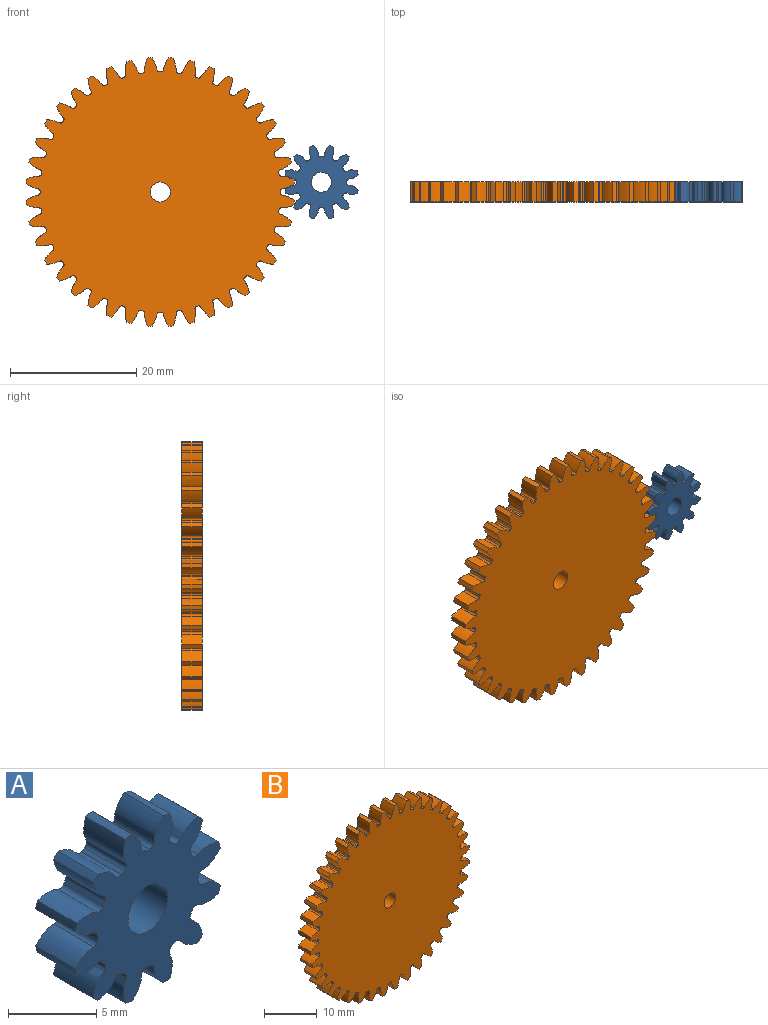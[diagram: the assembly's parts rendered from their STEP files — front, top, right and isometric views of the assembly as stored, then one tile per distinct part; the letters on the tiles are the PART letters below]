
ASSEMBLY  parts=2 mates=1
PART A: 75 faces, bbox 11.6x3.2x11.6 mm
  f0: cylinder r=5.93mm len=3.18mm, axis (0,1,0), area 1.7mm2, adj f11,f14,f60,f72
  f1: cylinder r=5.93mm len=3.18mm, axis (0,1,0), area 1.7mm2, adj f11,f14,f67,f70
  f2: cylinder r=5.93mm len=3.18mm, axis (0,1,0), area 1.7mm2, adj f11,f14,f55,f62
  f3: cylinder r=5.93mm len=3.18mm, axis (0,1,0), area 1.7mm2, adj f11,f14,f50,f57
  f4: cylinder r=5.93mm len=3.18mm, axis (0,1,0), area 1.7mm2, adj f11,f14,f45,f52
  f5: cylinder r=5.93mm len=3.18mm, axis (0,1,0), area 1.7mm2, adj f11,f14,f35,f47
  f6: cylinder r=5.93mm len=3.18mm, axis (0,1,0), area 1.7mm2, adj f11,f14,f15,f42
  f7: cylinder r=5.93mm len=3.18mm, axis (0,1,0), area 1.7mm2, adj f11,f14,f37,f40
  f8: cylinder r=5.93mm len=3.18mm, axis (0,1,0), area 1.7mm2, adj f11,f14,f25,f32
  f9: cylinder r=5.93mm len=3.18mm, axis (0,1,0), area 1.7mm2, adj f11,f14,f20,f27
  f10: cylinder r=5.93mm len=3.18mm, axis (0,1,0), area 1.7mm2, adj f11,f14,f22,f65
  f11: plane 11.6x11.6mm, normal (0,-1,0), area 70.2mm2, adj f0,f1,f2,f3,f4,f5,f6,f7
  f12: cylinder r=1.59mm len=3.18mm, axis (0,1,0), area 31.7mm2, adj f11,f14
  f13: cylinder r=5.93mm len=3.18mm, axis (0,1,0), area 1.7mm2, adj f11,f14,f17,f30
  f14: plane 11.6x11.6mm, normal (0,1,0), area 70.2mm2, adj f0,f1,f2,f3,f4,f5,f6,f7
  f15: extruded ~3.18x1.46mm, area 5.4mm2, adj f6,f11,f14,f18
  f16: cylinder r=4.02mm len=3.18mm, axis (0,1,0), area 0.9mm2, adj f11,f14,f18,f19
  f17: extruded ~3.18x1.46mm, area 5.4mm2, adj f11,f13,f14,f19
  f18: cylinder r=0.35mm len=3.18mm, axis (0,1,0), area 1.7mm2, adj f11,f14,f15,f16
  f19: cylinder r=0.35mm len=3.18mm, axis (0,1,0), area 1.7mm2, adj f11,f14,f16,f17
  f20: extruded ~3.18x1.46mm, area 5.4mm2, adj f9,f11,f14,f23
  f21: cylinder r=4.02mm len=3.18mm, axis (0,1,0), area 0.9mm2, adj f11,f14,f23,f24
  f22: extruded ~3.18x1.46mm, area 5.4mm2, adj f10,f11,f14,f24
  f23: cylinder r=0.35mm len=3.18mm, axis (0,1,0), area 1.7mm2, adj f11,f14,f20,f21
  f24: cylinder r=0.35mm len=3.18mm, axis (0,1,0), area 1.7mm2, adj f11,f14,f21,f22
  f25: extruded ~3.18x1.4mm, area 5.4mm2, adj f8,f11,f14,f28
  f26: cylinder r=4.02mm len=3.18mm, axis (0,1,0), area 0.9mm2, adj f11,f14,f28,f29
  f27: extruded ~3.18x1.65mm, area 5.4mm2, adj f9,f11,f14,f29
  f28: cylinder r=0.35mm len=3.18mm, axis (0,1,0), area 1.7mm2, adj f11,f14,f25,f26
  f29: cylinder r=0.35mm len=3.18mm, axis (0,1,0), area 1.7mm2, adj f11,f14,f26,f27
  f30: extruded ~3.18x1.65mm, area 5.4mm2, adj f11,f13,f14,f33
  f31: cylinder r=4.02mm len=3.18mm, axis (0,1,0), area 0.9mm2, adj f11,f14,f33,f34
  f32: extruded ~3.18x1.4mm, area 5.4mm2, adj f8,f11,f14,f34
  f33: cylinder r=0.35mm len=3.18mm, axis (0,1,0), area 1.7mm2, adj f11,f14,f30,f31
  f34: cylinder r=0.35mm len=3.18mm, axis (0,1,0), area 1.7mm2, adj f11,f14,f31,f32
  f35: extruded ~3.18x1.65mm, area 5.4mm2, adj f5,f11,f14,f38
  f36: cylinder r=4.02mm len=3.18mm, axis (0,1,0), area 0.9mm2, adj f11,f14,f38,f39
  f37: extruded ~3.18x1.4mm, area 5.4mm2, adj f7,f11,f14,f39
  f38: cylinder r=0.35mm len=3.18mm, axis (0,1,0), area 1.7mm2, adj f11,f14,f35,f36
  f39: cylinder r=0.35mm len=3.18mm, axis (0,1,0), area 1.7mm2, adj f11,f14,f36,f37
  f40: extruded ~3.18x1.4mm, area 5.4mm2, adj f7,f11,f14,f43
  f41: cylinder r=4.02mm len=3.18mm, axis (0,1,0), area 0.9mm2, adj f11,f14,f43,f44
  f42: extruded ~3.18x1.65mm, area 5.4mm2, adj f6,f11,f14,f44
  f43: cylinder r=0.35mm len=3.18mm, axis (0,1,0), area 1.7mm2, adj f11,f14,f40,f41
  f44: cylinder r=0.35mm len=3.18mm, axis (0,1,0), area 1.7mm2, adj f11,f14,f41,f42
  f45: extruded ~3.18x1.46mm, area 5.4mm2, adj f4,f11,f14,f48
  f46: cylinder r=4.02mm len=3.18mm, axis (0,1,0), area 0.9mm2, adj f11,f14,f48,f49
  f47: extruded ~3.18x1.46mm, area 5.4mm2, adj f5,f11,f14,f49
  f48: cylinder r=0.35mm len=3.18mm, axis (0,1,0), area 1.7mm2, adj f11,f14,f45,f46
  f49: cylinder r=0.35mm len=3.18mm, axis (0,1,0), area 1.7mm2, adj f11,f14,f46,f47
  f50: extruded ~3.18x1.4mm, area 5.4mm2, adj f3,f11,f14,f53
  f51: cylinder r=4.02mm len=3.18mm, axis (0,1,0), area 0.9mm2, adj f11,f14,f53,f54
  f52: extruded ~3.18x1.65mm, area 5.4mm2, adj f4,f11,f14,f54
  f53: cylinder r=0.35mm len=3.18mm, axis (0,1,0), area 1.7mm2, adj f11,f14,f50,f51
  f54: cylinder r=0.35mm len=3.18mm, axis (0,1,0), area 1.7mm2, adj f11,f14,f51,f52
  f55: extruded ~3.18x1.65mm, area 5.4mm2, adj f2,f11,f14,f58
  f56: cylinder r=4.02mm len=3.18mm, axis (0,1,0), area 0.9mm2, adj f11,f14,f58,f59
  f57: extruded ~3.18x1.4mm, area 5.4mm2, adj f3,f11,f14,f59
  f58: cylinder r=0.35mm len=3.18mm, axis (0,1,0), area 1.7mm2, adj f11,f14,f55,f56
  f59: cylinder r=0.35mm len=3.18mm, axis (0,1,0), area 1.7mm2, adj f11,f14,f56,f57
  f60: extruded ~3.18x1.46mm, area 5.4mm2, adj f0,f11,f14,f63
  f61: cylinder r=4.02mm len=3.18mm, axis (0,1,0), area 0.9mm2, adj f11,f14,f63,f64
  f62: extruded ~3.18x1.46mm, area 5.4mm2, adj f2,f11,f14,f64
  f63: cylinder r=0.35mm len=3.18mm, axis (0,1,0), area 1.7mm2, adj f11,f14,f60,f61
  f64: cylinder r=0.35mm len=3.18mm, axis (0,1,0), area 1.7mm2, adj f11,f14,f61,f62
  f65: extruded ~3.18x1.65mm, area 5.4mm2, adj f10,f11,f14,f68
  f66: cylinder r=4.02mm len=3.18mm, axis (0,1,0), area 0.9mm2, adj f11,f14,f68,f69
  f67: extruded ~3.18x1.4mm, area 5.4mm2, adj f1,f11,f14,f69
  f68: cylinder r=0.35mm len=3.18mm, axis (0,1,0), area 1.7mm2, adj f11,f14,f65,f66
  f69: cylinder r=0.35mm len=3.18mm, axis (0,1,0), area 1.7mm2, adj f11,f14,f66,f67
  f70: extruded ~3.18x1.4mm, area 5.4mm2, adj f1,f11,f14,f73
  f71: cylinder r=4.02mm len=3.18mm, axis (0,1,0), area 0.9mm2, adj f11,f14,f73,f74
  f72: extruded ~3.18x1.65mm, area 5.4mm2, adj f0,f11,f14,f74
  f73: cylinder r=0.35mm len=3.18mm, axis (0,1,0), area 1.7mm2, adj f11,f14,f70,f71
  f74: cylinder r=0.35mm len=3.18mm, axis (0,1,0), area 1.7mm2, adj f11,f14,f71,f72
PART B: 243 faces, bbox 42.6x3.2x42.6 mm
  f0: cylinder r=21.34mm len=3.18mm, axis (0,1,0), area 2.5mm2, adj f39,f42,f148,f240
  f1: cylinder r=21.34mm len=3.18mm, axis (0,1,0), area 2.5mm2, adj f39,f42,f235,f238
  f2: cylinder r=21.34mm len=3.18mm, axis (0,1,0), area 2.5mm2, adj f39,f42,f230,f233
  f3: cylinder r=21.34mm len=3.18mm, axis (0,1,0), area 2.5mm2, adj f39,f42,f225,f228
  f4: cylinder r=21.34mm len=3.18mm, axis (0,1,0), area 2.5mm2, adj f39,f42,f220,f223
  f5: cylinder r=21.34mm len=3.18mm, axis (0,1,0), area 2.5mm2, adj f39,f42,f215,f218
  f6: cylinder r=21.34mm len=3.18mm, axis (0,1,0), area 2.5mm2, adj f39,f42,f210,f213
  f7: cylinder r=21.34mm len=3.18mm, axis (0,1,0), area 2.5mm2, adj f39,f42,f205,f208
  f8: cylinder r=21.34mm len=3.18mm, axis (0,1,0), area 2.5mm2, adj f39,f42,f193,f200
  f9: cylinder r=21.34mm len=3.18mm, axis (0,1,0), area 2.5mm2, adj f39,f42,f195,f203
  f10: cylinder r=21.34mm len=3.18mm, axis (0,1,0), area 2.5mm2, adj f39,f42,f190,f198
  f11: cylinder r=21.34mm len=3.18mm, axis (0,1,0), area 2.5mm2, adj f39,f42,f185,f188
  f12: cylinder r=21.34mm len=3.18mm, axis (0,1,0), area 2.5mm2, adj f39,f42,f180,f183
  f13: cylinder r=21.34mm len=3.18mm, axis (0,1,0), area 2.5mm2, adj f39,f42,f175,f178
  f14: cylinder r=21.34mm len=3.18mm, axis (0,1,0), area 2.5mm2, adj f39,f42,f170,f173
  f15: cylinder r=21.34mm len=3.18mm, axis (0,1,0), area 2.5mm2, adj f39,f42,f165,f168
  f16: cylinder r=21.34mm len=3.18mm, axis (0,1,0), area 2.5mm2, adj f39,f42,f138,f160
  f17: cylinder r=21.34mm len=3.18mm, axis (0,1,0), area 2.5mm2, adj f39,f42,f155,f158
  f18: cylinder r=21.34mm len=3.18mm, axis (0,1,0), area 2.5mm2, adj f39,f42,f143,f150
  f19: cylinder r=21.34mm len=3.18mm, axis (0,1,0), area 2.5mm2, adj f39,f42,f145,f153
  f20: cylinder r=21.34mm len=3.18mm, axis (0,1,0), area 2.5mm2, adj f39,f42,f133,f140
  f21: cylinder r=21.34mm len=3.18mm, axis (0,1,0), area 2.5mm2, adj f39,f42,f128,f135
  f22: cylinder r=21.34mm len=3.18mm, axis (0,1,0), area 2.5mm2, adj f39,f42,f123,f130
  f23: cylinder r=21.34mm len=3.18mm, axis (0,1,0), area 2.5mm2, adj f39,f42,f83,f125
  f24: cylinder r=21.34mm len=3.18mm, axis (0,1,0), area 2.5mm2, adj f39,f42,f43,f120
  f25: cylinder r=21.34mm len=3.18mm, axis (0,1,0), area 2.5mm2, adj f39,f42,f115,f118
  f26: cylinder r=21.34mm len=3.18mm, axis (0,1,0), area 2.5mm2, adj f39,f42,f110,f113
  f27: cylinder r=21.34mm len=3.18mm, axis (0,1,0), area 2.5mm2, adj f39,f42,f105,f108
  f28: cylinder r=21.34mm len=3.18mm, axis (0,1,0), area 2.5mm2, adj f39,f42,f93,f100
  f29: cylinder r=21.34mm len=3.18mm, axis (0,1,0), area 2.5mm2, adj f39,f42,f95,f103
  f30: cylinder r=21.34mm len=3.18mm, axis (0,1,0), area 2.5mm2, adj f39,f42,f90,f98
  f31: cylinder r=21.34mm len=3.18mm, axis (0,1,0), area 2.5mm2, adj f39,f42,f85,f88
  f32: cylinder r=21.34mm len=3.18mm, axis (0,1,0), area 2.5mm2, adj f39,f42,f68,f80
  f33: cylinder r=21.34mm len=3.18mm, axis (0,1,0), area 2.5mm2, adj f39,f42,f75,f78
  f34: cylinder r=21.34mm len=3.18mm, axis (0,1,0), area 2.5mm2, adj f39,f42,f63,f70
  f35: cylinder r=21.34mm len=3.18mm, axis (0,1,0), area 2.5mm2, adj f39,f42,f65,f163
  f36: cylinder r=21.34mm len=3.18mm, axis (0,1,0), area 2.5mm2, adj f39,f42,f60,f73
  f37: cylinder r=21.34mm len=3.18mm, axis (0,1,0), area 2.5mm2, adj f39,f42,f55,f58
  f38: cylinder r=21.34mm len=3.18mm, axis (0,1,0), area 2.5mm2, adj f39,f42,f50,f53
  f39: plane 42.6x42.6mm, normal (0,-1,0), area 1279.5mm2, adj f0,f1,f2,f3,f4,f5,f6,f7
  f40: cylinder r=1.59mm len=3.18mm, axis (0,1,0), area 31.7mm2, adj f39,f42
  f41: cylinder r=21.34mm len=3.18mm, axis (0,1,0), area 2.5mm2, adj f39,f42,f45,f48
  f42: plane 42.6x42.6mm, normal (0,1,0), area 1279.5mm2, adj f0,f1,f2,f3,f4,f5,f6,f7
  f43: extruded ~3.18x1.96mm, area 6.7mm2, adj f24,f39,f42,f46
  f44: cylinder r=19.05mm len=3.18mm, axis (0,1,0), area 0.9mm2, adj f39,f42,f46,f47
  f45: extruded ~3.18x1.96mm, area 6.7mm2, adj f39,f41,f42,f47
  f46: cylinder r=0.36mm len=3.18mm, axis (0,1,0), area 1.6mm2, adj f39,f42,f43,f44
  f47: cylinder r=0.36mm len=3.18mm, axis (0,1,0), area 1.6mm2, adj f39,f42,f44,f45
  f48: extruded ~3.18x2.05mm, area 6.7mm2, adj f39,f41,f42,f51
  f49: cylinder r=19.05mm len=3.18mm, axis (0,1,0), area 0.9mm2, adj f39,f42,f51,f52
  f50: extruded ~3.18x1.81mm, area 6.7mm2, adj f38,f39,f42,f52
  f51: cylinder r=0.36mm len=3.18mm, axis (0,1,0), area 1.6mm2, adj f39,f42,f48,f49
  f52: cylinder r=0.36mm len=3.18mm, axis (0,1,0), area 1.6mm2, adj f39,f42,f49,f50
  f53: extruded ~3.18x2.1mm, area 6.7mm2, adj f38,f39,f42,f56
  f54: cylinder r=19.05mm len=3.18mm, axis (0,1,0), area 0.9mm2, adj f39,f42,f56,f57
  f55: extruded ~3.18x1.62mm, area 6.7mm2, adj f37,f39,f42,f57
  f56: cylinder r=0.36mm len=3.18mm, axis (0,1,0), area 1.6mm2, adj f39,f42,f53,f54
  f57: cylinder r=0.36mm len=3.18mm, axis (0,1,0), area 1.6mm2, adj f39,f42,f54,f55
  f58: extruded ~3.18x2.1mm, area 6.7mm2, adj f37,f39,f42,f61
  f59: cylinder r=19.05mm len=3.18mm, axis (0,1,0), area 0.9mm2, adj f39,f42,f61,f62
  f60: extruded ~3.18x1.59mm, area 6.7mm2, adj f36,f39,f42,f62
  f61: cylinder r=0.36mm len=3.18mm, axis (0,1,0), area 1.6mm2, adj f39,f42,f58,f59
  f62: cylinder r=0.36mm len=3.18mm, axis (0,1,0), area 1.6mm2, adj f39,f42,f59,f60
  f63: extruded ~3.18x1.59mm, area 6.7mm2, adj f34,f39,f42,f66
  f64: cylinder r=19.05mm len=3.18mm, axis (0,1,0), area 0.9mm2, adj f39,f42,f66,f67
  f65: extruded ~3.18x2.1mm, area 6.7mm2, adj f35,f39,f42,f67
  f66: cylinder r=0.36mm len=3.18mm, axis (0,1,0), area 1.6mm2, adj f39,f42,f63,f64
  f67: cylinder r=0.36mm len=3.18mm, axis (0,1,0), area 1.6mm2, adj f39,f42,f64,f65
  f68: extruded ~3.18x1.79mm, area 6.7mm2, adj f32,f39,f42,f71
  f69: cylinder r=19.05mm len=3.18mm, axis (0,1,0), area 0.9mm2, adj f39,f42,f71,f72
  f70: extruded ~3.18x2.05mm, area 6.7mm2, adj f34,f39,f42,f72
  f71: cylinder r=0.36mm len=3.18mm, axis (0,1,0), area 1.6mm2, adj f39,f42,f68,f69
  f72: cylinder r=0.36mm len=3.18mm, axis (0,1,0), area 1.6mm2, adj f39,f42,f69,f70
  f73: extruded ~3.18x2.05mm, area 6.7mm2, adj f36,f39,f42,f76
  f74: cylinder r=19.05mm len=3.18mm, axis (0,1,0), area 0.9mm2, adj f39,f42,f76,f77
  f75: extruded ~3.18x1.79mm, area 6.7mm2, adj f33,f39,f42,f77
  f76: cylinder r=0.36mm len=3.18mm, axis (0,1,0), area 1.6mm2, adj f39,f42,f73,f74
  f77: cylinder r=0.36mm len=3.18mm, axis (0,1,0), area 1.6mm2, adj f39,f42,f74,f75
  f78: extruded ~3.18x1.94mm, area 6.7mm2, adj f33,f39,f42,f81
  f79: cylinder r=19.05mm len=3.18mm, axis (0,1,0), area 0.9mm2, adj f39,f42,f81,f82
  f80: extruded ~3.18x1.94mm, area 6.7mm2, adj f32,f39,f42,f82
  f81: cylinder r=0.36mm len=3.18mm, axis (0,1,0), area 1.6mm2, adj f39,f42,f78,f79
  f82: cylinder r=0.36mm len=3.18mm, axis (0,1,0), area 1.6mm2, adj f39,f42,f79,f80
  f83: extruded ~3.18x2.1mm, area 6.7mm2, adj f23,f39,f42,f86
  f84: cylinder r=19.05mm len=3.18mm, axis (0,1,0), area 0.9mm2, adj f39,f42,f86,f87
  f85: extruded ~3.18x1.62mm, area 6.7mm2, adj f31,f39,f42,f87
  f86: cylinder r=0.36mm len=3.18mm, axis (0,1,0), area 1.6mm2, adj f39,f42,f83,f84
  f87: cylinder r=0.36mm len=3.18mm, axis (0,1,0), area 1.6mm2, adj f39,f42,f84,f85
  f88: extruded ~3.18x2.1mm, area 6.7mm2, adj f31,f39,f42,f91
  f89: cylinder r=19.05mm len=3.18mm, axis (0,1,0), area 0.9mm2, adj f39,f42,f91,f92
  f90: extruded ~3.18x1.59mm, area 6.7mm2, adj f30,f39,f42,f92
  f91: cylinder r=0.36mm len=3.18mm, axis (0,1,0), area 1.6mm2, adj f39,f42,f88,f89
  f92: cylinder r=0.36mm len=3.18mm, axis (0,1,0), area 1.6mm2, adj f39,f42,f89,f90
  f93: extruded ~3.18x1.94mm, area 6.7mm2, adj f28,f39,f42,f96
  f94: cylinder r=19.05mm len=3.18mm, axis (0,1,0), area 0.9mm2, adj f39,f42,f96,f97
  f95: extruded ~3.18x1.94mm, area 6.7mm2, adj f29,f39,f42,f97
  f96: cylinder r=0.36mm len=3.18mm, axis (0,1,0), area 1.6mm2, adj f39,f42,f93,f94
  f97: cylinder r=0.36mm len=3.18mm, axis (0,1,0), area 1.6mm2, adj f39,f42,f94,f95
  f98: extruded ~3.18x2.05mm, area 6.7mm2, adj f30,f39,f42,f101
  f99: cylinder r=19.05mm len=3.18mm, axis (0,1,0), area 0.9mm2, adj f39,f42,f101,f102
  f100: extruded ~3.18x1.79mm, area 6.7mm2, adj f28,f39,f42,f102
  f101: cylinder r=0.36mm len=3.18mm, axis (0,1,0), area 1.6mm2, adj f39,f42,f98,f99
  f102: cylinder r=0.36mm len=3.18mm, axis (0,1,0), area 1.6mm2, adj f39,f42,f99,f100
  f103: extruded ~3.18x1.79mm, area 6.7mm2, adj f29,f39,f42,f106
  f104: cylinder r=19.05mm len=3.18mm, axis (0,1,0), area 0.9mm2, adj f39,f42,f106,f107
  f105: extruded ~3.18x2.05mm, area 6.7mm2, adj f27,f39,f42,f107
  f106: cylinder r=0.36mm len=3.18mm, axis (0,1,0), area 1.6mm2, adj f39,f42,f103,f104
  f107: cylinder r=0.36mm len=3.18mm, axis (0,1,0), area 1.6mm2, adj f39,f42,f104,f105
  f108: extruded ~3.18x1.59mm, area 6.7mm2, adj f27,f39,f42,f111
  f109: cylinder r=19.05mm len=3.18mm, axis (0,1,0), area 0.9mm2, adj f39,f42,f111,f112
  f110: extruded ~3.18x2.1mm, area 6.7mm2, adj f26,f39,f42,f112
  f111: cylinder r=0.36mm len=3.18mm, axis (0,1,0), area 1.6mm2, adj f39,f42,f108,f109
  f112: cylinder r=0.36mm len=3.18mm, axis (0,1,0), area 1.6mm2, adj f39,f42,f109,f110
  f113: extruded ~3.18x1.62mm, area 6.7mm2, adj f26,f39,f42,f116
  f114: cylinder r=19.05mm len=3.18mm, axis (0,1,0), area 0.9mm2, adj f39,f42,f116,f117
  f115: extruded ~3.18x2.1mm, area 6.7mm2, adj f25,f39,f42,f117
  f116: cylinder r=0.36mm len=3.18mm, axis (0,1,0), area 1.6mm2, adj f39,f42,f113,f114
  f117: cylinder r=0.36mm len=3.18mm, axis (0,1,0), area 1.6mm2, adj f39,f42,f114,f115
  f118: extruded ~3.18x1.81mm, area 6.7mm2, adj f25,f39,f42,f121
  f119: cylinder r=19.05mm len=3.18mm, axis (0,1,0), area 0.9mm2, adj f39,f42,f121,f122
  f120: extruded ~3.18x2.05mm, area 6.7mm2, adj f24,f39,f42,f122
  f121: cylinder r=0.36mm len=3.18mm, axis (0,1,0), area 1.6mm2, adj f39,f42,f118,f119
  f122: cylinder r=0.36mm len=3.18mm, axis (0,1,0), area 1.6mm2, adj f39,f42,f119,f120
  f123: extruded ~3.18x2.05mm, area 6.7mm2, adj f22,f39,f42,f126
  f124: cylinder r=19.05mm len=3.18mm, axis (0,1,0), area 0.9mm2, adj f39,f42,f126,f127
  f125: extruded ~3.18x1.81mm, area 6.7mm2, adj f23,f39,f42,f127
  f126: cylinder r=0.36mm len=3.18mm, axis (0,1,0), area 1.6mm2, adj f39,f42,f123,f124
  f127: cylinder r=0.36mm len=3.18mm, axis (0,1,0), area 1.6mm2, adj f39,f42,f124,f125
  f128: extruded ~3.18x1.96mm, area 6.7mm2, adj f21,f39,f42,f131
  f129: cylinder r=19.05mm len=3.18mm, axis (0,1,0), area 0.9mm2, adj f39,f42,f131,f132
  f130: extruded ~3.18x1.96mm, area 6.7mm2, adj f22,f39,f42,f132
  f131: cylinder r=0.36mm len=3.18mm, axis (0,1,0), area 1.6mm2, adj f39,f42,f128,f129
  f132: cylinder r=0.36mm len=3.18mm, axis (0,1,0), area 1.6mm2, adj f39,f42,f129,f130
  f133: extruded ~3.18x1.81mm, area 6.7mm2, adj f20,f39,f42,f136
  f134: cylinder r=19.05mm len=3.18mm, axis (0,1,0), area 0.9mm2, adj f39,f42,f136,f137
  f135: extruded ~3.18x2.05mm, area 6.7mm2, adj f21,f39,f42,f137
  f136: cylinder r=0.36mm len=3.18mm, axis (0,1,0), area 1.6mm2, adj f39,f42,f133,f134
  f137: cylinder r=0.36mm len=3.18mm, axis (0,1,0), area 1.6mm2, adj f39,f42,f134,f135
  f138: extruded ~3.18x1.62mm, area 6.7mm2, adj f16,f39,f42,f141
  f139: cylinder r=19.05mm len=3.18mm, axis (0,1,0), area 0.9mm2, adj f39,f42,f141,f142
  f140: extruded ~3.18x2.1mm, area 6.7mm2, adj f20,f39,f42,f142
  f141: cylinder r=0.36mm len=3.18mm, axis (0,1,0), area 1.6mm2, adj f39,f42,f138,f139
  f142: cylinder r=0.36mm len=3.18mm, axis (0,1,0), area 1.6mm2, adj f39,f42,f139,f140
  f143: extruded ~3.18x1.94mm, area 6.7mm2, adj f18,f39,f42,f146
  f144: cylinder r=19.05mm len=3.18mm, axis (0,1,0), area 0.9mm2, adj f39,f42,f146,f147
  f145: extruded ~3.18x1.94mm, area 6.7mm2, adj f19,f39,f42,f147
  f146: cylinder r=0.36mm len=3.18mm, axis (0,1,0), area 1.6mm2, adj f39,f42,f143,f144
  f147: cylinder r=0.36mm len=3.18mm, axis (0,1,0), area 1.6mm2, adj f39,f42,f144,f145
  f148: extruded ~3.18x2.05mm, area 6.7mm2, adj f0,f39,f42,f151
  f149: cylinder r=19.05mm len=3.18mm, axis (0,1,0), area 0.9mm2, adj f39,f42,f151,f152
  f150: extruded ~3.18x1.79mm, area 6.7mm2, adj f18,f39,f42,f152
  f151: cylinder r=0.36mm len=3.18mm, axis (0,1,0), area 1.6mm2, adj f39,f42,f148,f149
  f152: cylinder r=0.36mm len=3.18mm, axis (0,1,0), area 1.6mm2, adj f39,f42,f149,f150
  f153: extruded ~3.18x1.79mm, area 6.7mm2, adj f19,f39,f42,f156
  f154: cylinder r=19.05mm len=3.18mm, axis (0,1,0), area 0.9mm2, adj f39,f42,f156,f157
  f155: extruded ~3.18x2.05mm, area 6.7mm2, adj f17,f39,f42,f157
  f156: cylinder r=0.36mm len=3.18mm, axis (0,1,0), area 1.6mm2, adj f39,f42,f153,f154
  f157: cylinder r=0.36mm len=3.18mm, axis (0,1,0), area 1.6mm2, adj f39,f42,f154,f155
  f158: extruded ~3.18x1.59mm, area 6.7mm2, adj f17,f39,f42,f161
  f159: cylinder r=19.05mm len=3.18mm, axis (0,1,0), area 0.9mm2, adj f39,f42,f161,f162
  f160: extruded ~3.18x2.1mm, area 6.7mm2, adj f16,f39,f42,f162
  f161: cylinder r=0.36mm len=3.18mm, axis (0,1,0), area 1.6mm2, adj f39,f42,f158,f159
  f162: cylinder r=0.36mm len=3.18mm, axis (0,1,0), area 1.6mm2, adj f39,f42,f159,f160
  f163: extruded ~3.18x1.62mm, area 6.7mm2, adj f35,f39,f42,f166
  f164: cylinder r=19.05mm len=3.18mm, axis (0,1,0), area 0.9mm2, adj f39,f42,f166,f167
  f165: extruded ~3.18x2.1mm, area 6.7mm2, adj f15,f39,f42,f167
  f166: cylinder r=0.36mm len=3.18mm, axis (0,1,0), area 1.6mm2, adj f39,f42,f163,f164
  f167: cylinder r=0.36mm len=3.18mm, axis (0,1,0), area 1.6mm2, adj f39,f42,f164,f165
  f168: extruded ~3.18x1.81mm, area 6.7mm2, adj f15,f39,f42,f171
  f169: cylinder r=19.05mm len=3.18mm, axis (0,1,0), area 0.9mm2, adj f39,f42,f171,f172
  f170: extruded ~3.18x2.05mm, area 6.7mm2, adj f14,f39,f42,f172
  f171: cylinder r=0.36mm len=3.18mm, axis (0,1,0), area 1.6mm2, adj f39,f42,f168,f169
  f172: cylinder r=0.36mm len=3.18mm, axis (0,1,0), area 1.6mm2, adj f39,f42,f169,f170
  f173: extruded ~3.18x1.96mm, area 6.7mm2, adj f14,f39,f42,f176
  f174: cylinder r=19.05mm len=3.18mm, axis (0,1,0), area 0.9mm2, adj f39,f42,f176,f177
  f175: extruded ~3.18x1.96mm, area 6.7mm2, adj f13,f39,f42,f177
  f176: cylinder r=0.36mm len=3.18mm, axis (0,1,0), area 1.6mm2, adj f39,f42,f173,f174
  f177: cylinder r=0.36mm len=3.18mm, axis (0,1,0), area 1.6mm2, adj f39,f42,f174,f175
  f178: extruded ~3.18x2.05mm, area 6.7mm2, adj f13,f39,f42,f181
  f179: cylinder r=19.05mm len=3.18mm, axis (0,1,0), area 0.9mm2, adj f39,f42,f181,f182
  f180: extruded ~3.18x1.81mm, area 6.7mm2, adj f12,f39,f42,f182
  f181: cylinder r=0.36mm len=3.18mm, axis (0,1,0), area 1.6mm2, adj f39,f42,f178,f179
  f182: cylinder r=0.36mm len=3.18mm, axis (0,1,0), area 1.6mm2, adj f39,f42,f179,f180
  f183: extruded ~3.18x2.1mm, area 6.7mm2, adj f12,f39,f42,f186
  f184: cylinder r=19.05mm len=3.18mm, axis (0,1,0), area 0.9mm2, adj f39,f42,f186,f187
  f185: extruded ~3.18x1.62mm, area 6.7mm2, adj f11,f39,f42,f187
  f186: cylinder r=0.36mm len=3.18mm, axis (0,1,0), area 1.6mm2, adj f39,f42,f183,f184
  f187: cylinder r=0.36mm len=3.18mm, axis (0,1,0), area 1.6mm2, adj f39,f42,f184,f185
  f188: extruded ~3.18x2.1mm, area 6.7mm2, adj f11,f39,f42,f191
  f189: cylinder r=19.05mm len=3.18mm, axis (0,1,0), area 0.9mm2, adj f39,f42,f191,f192
  f190: extruded ~3.18x1.59mm, area 6.7mm2, adj f10,f39,f42,f192
  f191: cylinder r=0.36mm len=3.18mm, axis (0,1,0), area 1.6mm2, adj f39,f42,f188,f189
  f192: cylinder r=0.36mm len=3.18mm, axis (0,1,0), area 1.6mm2, adj f39,f42,f189,f190
  f193: extruded ~3.18x1.94mm, area 6.7mm2, adj f8,f39,f42,f196
  f194: cylinder r=19.05mm len=3.18mm, axis (0,1,0), area 0.9mm2, adj f39,f42,f196,f197
  f195: extruded ~3.18x1.94mm, area 6.7mm2, adj f9,f39,f42,f197
  f196: cylinder r=0.36mm len=3.18mm, axis (0,1,0), area 1.6mm2, adj f39,f42,f193,f194
  f197: cylinder r=0.36mm len=3.18mm, axis (0,1,0), area 1.6mm2, adj f39,f42,f194,f195
  f198: extruded ~3.18x2.05mm, area 6.7mm2, adj f10,f39,f42,f201
  f199: cylinder r=19.05mm len=3.18mm, axis (0,1,0), area 0.9mm2, adj f39,f42,f201,f202
  f200: extruded ~3.18x1.79mm, area 6.7mm2, adj f8,f39,f42,f202
  f201: cylinder r=0.36mm len=3.18mm, axis (0,1,0), area 1.6mm2, adj f39,f42,f198,f199
  f202: cylinder r=0.36mm len=3.18mm, axis (0,1,0), area 1.6mm2, adj f39,f42,f199,f200
  f203: extruded ~3.18x1.79mm, area 6.7mm2, adj f9,f39,f42,f206
  f204: cylinder r=19.05mm len=3.18mm, axis (0,1,0), area 0.9mm2, adj f39,f42,f206,f207
  f205: extruded ~3.18x2.05mm, area 6.7mm2, adj f7,f39,f42,f207
  f206: cylinder r=0.36mm len=3.18mm, axis (0,1,0), area 1.6mm2, adj f39,f42,f203,f204
  f207: cylinder r=0.36mm len=3.18mm, axis (0,1,0), area 1.6mm2, adj f39,f42,f204,f205
  f208: extruded ~3.18x1.59mm, area 6.7mm2, adj f7,f39,f42,f211
  f209: cylinder r=19.05mm len=3.18mm, axis (0,1,0), area 0.9mm2, adj f39,f42,f211,f212
  f210: extruded ~3.18x2.1mm, area 6.7mm2, adj f6,f39,f42,f212
  f211: cylinder r=0.36mm len=3.18mm, axis (0,1,0), area 1.6mm2, adj f39,f42,f208,f209
  f212: cylinder r=0.36mm len=3.18mm, axis (0,1,0), area 1.6mm2, adj f39,f42,f209,f210
  f213: extruded ~3.18x1.62mm, area 6.7mm2, adj f6,f39,f42,f216
  f214: cylinder r=19.05mm len=3.18mm, axis (0,1,0), area 0.9mm2, adj f39,f42,f216,f217
  f215: extruded ~3.18x2.1mm, area 6.7mm2, adj f5,f39,f42,f217
  f216: cylinder r=0.36mm len=3.18mm, axis (0,1,0), area 1.6mm2, adj f39,f42,f213,f214
  f217: cylinder r=0.36mm len=3.18mm, axis (0,1,0), area 1.6mm2, adj f39,f42,f214,f215
  f218: extruded ~3.18x1.81mm, area 6.7mm2, adj f5,f39,f42,f221
  f219: cylinder r=19.05mm len=3.18mm, axis (0,1,0), area 0.9mm2, adj f39,f42,f221,f222
  f220: extruded ~3.18x2.05mm, area 6.7mm2, adj f4,f39,f42,f222
  f221: cylinder r=0.36mm len=3.18mm, axis (0,1,0), area 1.6mm2, adj f39,f42,f218,f219
  f222: cylinder r=0.36mm len=3.18mm, axis (0,1,0), area 1.6mm2, adj f39,f42,f219,f220
  f223: extruded ~3.18x1.96mm, area 6.7mm2, adj f4,f39,f42,f226
  f224: cylinder r=19.05mm len=3.18mm, axis (0,1,0), area 0.9mm2, adj f39,f42,f226,f227
  f225: extruded ~3.18x1.96mm, area 6.7mm2, adj f3,f39,f42,f227
  f226: cylinder r=0.36mm len=3.18mm, axis (0,1,0), area 1.6mm2, adj f39,f42,f223,f224
  f227: cylinder r=0.36mm len=3.18mm, axis (0,1,0), area 1.6mm2, adj f39,f42,f224,f225
  f228: extruded ~3.18x2.05mm, area 6.7mm2, adj f3,f39,f42,f231
  f229: cylinder r=19.05mm len=3.18mm, axis (0,1,0), area 0.9mm2, adj f39,f42,f231,f232
  f230: extruded ~3.18x1.81mm, area 6.7mm2, adj f2,f39,f42,f232
  f231: cylinder r=0.36mm len=3.18mm, axis (0,1,0), area 1.6mm2, adj f39,f42,f228,f229
  f232: cylinder r=0.36mm len=3.18mm, axis (0,1,0), area 1.6mm2, adj f39,f42,f229,f230
  f233: extruded ~3.18x2.1mm, area 6.7mm2, adj f2,f39,f42,f236
  f234: cylinder r=19.05mm len=3.18mm, axis (0,1,0), area 0.9mm2, adj f39,f42,f236,f237
  f235: extruded ~3.18x1.62mm, area 6.7mm2, adj f1,f39,f42,f237
  f236: cylinder r=0.36mm len=3.18mm, axis (0,1,0), area 1.6mm2, adj f39,f42,f233,f234
  f237: cylinder r=0.36mm len=3.18mm, axis (0,1,0), area 1.6mm2, adj f39,f42,f234,f235
  f238: extruded ~3.18x2.1mm, area 6.7mm2, adj f1,f39,f42,f241
  f239: cylinder r=19.05mm len=3.18mm, axis (0,1,0), area 0.9mm2, adj f39,f42,f241,f242
  f240: extruded ~3.18x1.59mm, area 6.7mm2, adj f0,f39,f42,f242
  f241: cylinder r=0.36mm len=3.18mm, axis (0,1,0), area 1.6mm2, adj f39,f42,f238,f239
  f242: cylinder r=0.36mm len=3.18mm, axis (0,1,0), area 1.6mm2, adj f39,f42,f239,f240
PLACE A t=(-0.14,-8.12,-10.67)mm
PLACE B t=(-25.71,-8.12,-12.22)mm
MATE revolute B.f39 <-> A.f11  axis (0,-1,0) through (-4.47,-11.29,-10.16)mm
